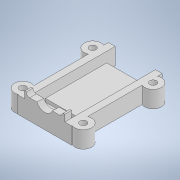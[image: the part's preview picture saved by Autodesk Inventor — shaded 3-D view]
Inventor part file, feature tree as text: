
AUTODESK INVENTOR PART (.ipt)
format: ipt  version: 2020.4 (Build 244396000, 396)  size: 212,480 bytes
history: native  units: mm
features: extrude x7, sketch x7, projected_geometry x1
ambient origin geometry x8: Origin, YZ Plane, XZ Plane, XY Plane, X Axis, Y Axis, Z Axis, Center Point
bodies: Solid1 (feature_tree)
feature tree (15):
  extrude  "Extrusion1"  Depth=27.0mm
  extrude  "Extrusion2"  Depth=2.0mm
  extrude  "Extrusion3"  Depth=2.0mm
  extrude  "Extrusion4"  Depth=5.0mm
  extrude  "Extrusion7"  Depth=5.0mm
  extrude  "Extrusion8"  Depth=2.0mm
  extrude  "Extrusion9"  Depth=10.0mm TaperAngle=0.0deg
  sketch  "Sketch1"  dims[d0=16.0mm d1=27.0mm]
  sketch  "Sketch2"  dims[d2=2.0mm d3=0.0mm d4=2.0mm]
  sketch  "Sketch3"  dims[d5=2.0mm d6=2.0mm]
  projected_geometry  "Projected Loop1"
  sketch  "Sketch4"  dims[d7=3.0mm d8=0.0mm d9=5.0mm]
  sketch  "Sketch8"  dims[d10=5.0mm d11=9.0mm]
  sketch  "Sketch9"  dims[d12=2.0mm d13=2.0mm]
  sketch  "Sketch10"  dims[d14=2.0mm d15=0.0mm d16=10.0mm d17=0.0mm d28=22.5mm d29=10.0mm d30=0.0mm d31=1.0mm d32=3.2mm d33=1.0mm d34=0.0mm d35=2.0mm d36=1.5mm d37=27.0mm d38=16.0mm d39=20.0mm d41=20.8mm d42=20.0mm d44=18.0mm d47=10.0mm d48=0.0mm]
